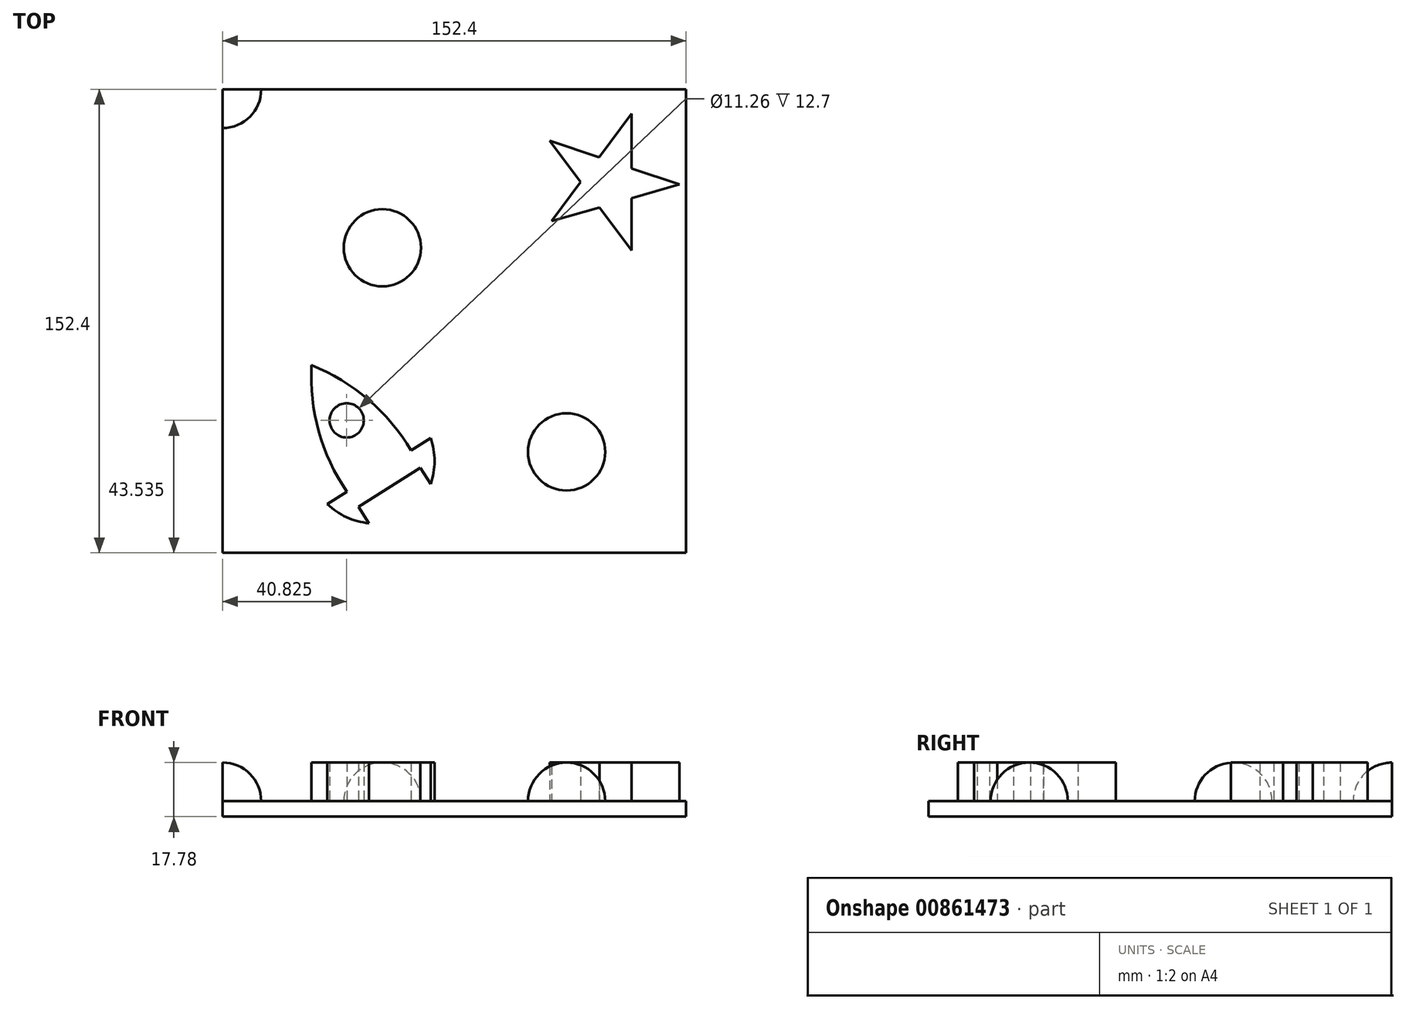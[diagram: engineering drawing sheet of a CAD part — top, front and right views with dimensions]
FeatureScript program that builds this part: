
annotation { "Feature Type Name" : "Feature", "Feature Type Description" : "" }
export const myFeature = defineFeature(function(context is Context, id is Id, definition is map)
    precondition{}
    {
        {
            var Q0;
            Q0=qCreatedBy(makeId("Top.planeOp"),FACE);
            var sketch = newSketch(context, id + "F0", { "sketchPlane" : qUnion([Q0])});
            skLineSegment(sketch, "E0.bottom", {"start": v(76.2, -76.2) * mm, "end": v(-76.2, -76.2) * mm});
            skLineSegment(sketch, "E0.top", {"start": v(76.2, 76.2) * mm, "end": v(-76.2, 76.2) * mm});
            skLineSegment(sketch, "E0.left", {"start": v(76.2, -76.2) * mm, "end": v(76.2, 76.2) * mm});
            skLineSegment(sketch, "E0.right", {"start": v(-76.2, -76.2) * mm, "end": v(-76.2, 76.2) * mm});
            skPoint(sketch, "E0.middle", {"position": v(0, 0) * mm});
            skLineSegment(sketch, "E1", {"start": v(0, 76.2) * mm, "end": v(0, -76.2) * mm, "construction": true});
            skLineSegment(sketch, "E2", {"start": v(-76.2, 0) * mm, "end": v(76.2, 0) * mm, "construction": true});
            skSolve(sketch);
        }
        {
            assignVariable(context, id + "F1", {"name" : "height", "anyValue" : 5.08 * mm});
        }
        {
            var Q0;
            Q0=makeQuery(id+"F0.imprint","IMPRINT",FACE,{"disambiguationData":[TD([[makeQuery(id+"F0.imprint","IMPRINT",EDGE,{"derivedFrom":sQuery(id+"F0.wireOp",EDGE,"E0.bottom")}),-1.0]])]});
            extrude(context, id + "F2", {"entities" : qUnion([Q0]), "depth" : getVariable(context, 'height'), "offsetDistance" : 25.4 * mm});
        }
        {
            assignVariable(context, id + "F3", {"name" : "height2", "anyValue" : 12.7 * mm});
        }
        {
            var Q0;
            Q0=makeQuery(id+"F2.opExtrude","CAP_FACE",FACE,{"disambiguationData":[OSD([sQuery(id+"F0.wireOp",EDGE,"E0.bottom"),sQuery(id+"F0.wireOp",EDGE,"E0.top"),sQuery(id+"F0.wireOp",EDGE,"E0.left"),sQuery(id+"F0.wireOp",EDGE,"E0.right")])],"isStart":false});
            var sketch = newSketch(context, id + "F4", { "sketchPlane" : qUnion([Q0])});
            skArc(sketch, "E3", {"start": v(49.62, -43.02) * mm, "mid": v(36.92, -30.32) * mm, "end": v(24.22, -43.02) * mm});
            skArc(sketch, "E4", {"start": v(-76.2, 63.5) * mm, "mid": v(-67.22, 67.22) * mm, "end": v(-63.5, 76.2) * mm});
            skLineSegment(sketch, "E5", {"start": v(49.62, -43.02) * mm, "end": v(24.22, -43.02) * mm});
            skLineSegment(sketch, "E6", {"start": v(-36.35, 24.1) * mm, "end": v(-10.95, 24.1) * mm});
            skArc(sketch, "E7", {"start": v(-10.95, 24.1) * mm, "mid": v(-23.65, 36.8) * mm, "end": v(-36.35, 24.1) * mm});
            skLineSegment(sketch, "E8", {"start": v(31.39, 59.27) * mm, "end": v(47.57, 53.82) * mm});
            skLineSegment(sketch, "E9", {"start": v(74, 44.9) * mm, "end": v(58.26, 40.4) * mm});
            skLineSegment(sketch, "E10", {"start": v(31.97, 32.85) * mm, "end": v(41.52, 45.68) * mm});
            skLineSegment(sketch, "E11", {"start": v(58.26, 68.18) * mm, "end": v(58.26, 50.22) * mm});
            skLineSegment(sketch, "E12", {"start": v(58.26, 23.21) * mm, "end": v(47.71, 37.37) * mm});
            skLineSegment(sketch, "E13.trimOffspring", {"start": v(41.52, 45.68) * mm, "end": v(31.39, 59.27) * mm});
            skLineSegment(sketch, "E14.trimOffspring", {"start": v(47.71, 37.37) * mm, "end": v(31.97, 32.85) * mm});
            skLineSegment(sketch, "E15.trimOffspring", {"start": v(58.26, 40.4) * mm, "end": v(58.26, 23.21) * mm});
            skLineSegment(sketch, "E16.trimOffspring", {"start": v(58.26, 50.22) * mm, "end": v(74, 44.9) * mm});
            skLineSegment(sketch, "E17.trimOffspring", {"start": v(47.57, 53.82) * mm, "end": v(58.26, 68.18) * mm});
            skLineSegment(sketch, "E18", {"start": v(-31.46, -61.14) * mm, "end": v(-11.2, -48.23) * mm});
            skLineSegment(sketch, "E19", {"start": v(-21.33, -54.69) * mm, "end": v(-46.94, -14.53) * mm, "construction": true});
            skArc(sketch, "E20", {"start": v(-46.94, -14.53) * mm, "mid": v(-43.64, -39.3) * mm, "end": v(-31.46, -61.14) * mm});
            skArc(sketch, "E21", {"start": v(-11.2, -48.23) * mm, "mid": v(-25.87, -27.98) * mm, "end": v(-46.94, -14.53) * mm});
            skLineSegment(sketch, "E22", {"start": v(-11.2, -48.23) * mm, "end": v(-7.8, -53.58) * mm});
            skLineSegment(sketch, "E23", {"start": v(-31.46, -61.14) * mm, "end": v(-28.04, -66.5) * mm});
            skLineSegment(sketch, "E24", {"start": v(-14.18, -42.6) * mm, "end": v(-35.31, -56.07) * mm, "construction": true});
            skLineSegment(sketch, "E25", {"start": v(-14.18, -42.6) * mm, "end": v(-7.72, -38.48) * mm});
            skLineSegment(sketch, "E26", {"start": v(-35.31, -56.07) * mm, "end": v(-41.77, -60.19) * mm});
            skArc(sketch, "E27", {"start": v(-7.8, -53.58) * mm, "mid": v(-6.5, -46.04) * mm, "end": v(-7.72, -38.48) * mm});
            skArc(sketch, "E28", {"start": v(-41.77, -60.19) * mm, "mid": v(-35.43, -64.49) * mm, "end": v(-28.04, -66.5) * mm});
            skCircle(sketch, "E29", {"center": v(-35.38, -32.66) * mm, "radius": 5.63 * mm});
            skSolve(sketch);
        }
        {
            var Q0;
            {var subQ0=sQuery(id+"F4.wireOp",EDGE,"E4");var subQ1=makeQuery(id+"F2.opExtrude","CAP_EDGE",EDGE,{"disambiguationData":[OSD([sQuery(id+"F0.wireOp",EDGE,"E0.right")])],"isStart":false});var subQ2=makeQuery(id+"F4.imprint","INTERSECT",VERTEX,{"derivedFrom":[subQ1,subQ0]});Q0=makeQuery(id+"F4.imprint","IMPRINT",FACE,{"disambiguationData":[TD([[makeQuery(id+"F4.imprint","IMPRINT",EDGE,{"disambiguationData":[TD([[subQ2,-1.0]])],"derivedFrom":subQ0}),1.0]])]});}
            var Q1;
            Q1=makeQuery(id+"F2.opExtrude","CAP_EDGE",EDGE,{"disambiguationData":[OSD([sQuery(id+"F0.wireOp",EDGE,"E0.right")])],"isStart":false});
            revolve(context, id + "F5", {"operationType" : NewBodyOperationType.ADD, "surfaceOperationType" : NewSurfaceOperationType.NEW, "entities" : qUnion([Q0]), "axis" : qUnion([Q1]), "revolveType" : RevolveType.ONE_DIRECTION, "oppositeDirection" : true, "angle" : 90 * degree});
        }
        {
            var Q0;
            Q0=makeQuery(id+"F4.imprint","IMPRINT",FACE,{"disambiguationData":[TD([[makeQuery(id+"F4.imprint","IMPRINT",EDGE,{"derivedFrom":sQuery(id+"F4.wireOp",EDGE,"E3")}),1.0]])]});
            var Q1;
            Q1=sQuery(id+"F4.wireOp",EDGE,"E5");
            revolve(context, id + "F6", {"operationType" : NewBodyOperationType.ADD, "surfaceOperationType" : NewSurfaceOperationType.NEW, "entities" : qUnion([Q0]), "axis" : qUnion([Q1]), "revolveType" : RevolveType.ONE_DIRECTION, "oppositeDirection" : true, "angle" : 180 * degree});
        }
        {
            var Q0;
            Q0=makeQuery(id+"F4.imprint","IMPRINT",FACE,{"disambiguationData":[TD([[makeQuery(id+"F4.imprint","IMPRINT",EDGE,{"derivedFrom":sQuery(id+"F4.wireOp",EDGE,"E6")}),1.0]])]});
            var Q1;
            Q1=sQuery(id+"F4.wireOp",EDGE,"E6");
            revolve(context, id + "F7", {"operationType" : NewBodyOperationType.ADD, "surfaceOperationType" : NewSurfaceOperationType.NEW, "entities" : qUnion([Q0]), "axis" : qUnion([Q1]), "revolveType" : RevolveType.ONE_DIRECTION, "angle" : 180 * degree});
        }
        {
            var Q0;
            Q0=makeQuery(id+"F4.imprint","IMPRINT",FACE,{"disambiguationData":[TD([[makeQuery(id+"F4.imprint","IMPRINT",EDGE,{"derivedFrom":sQuery(id+"F4.wireOp",EDGE,"E8")}),-1.0]])]});
            var Q1;
            {var subQ1=sQuery(id+"F4.wireOp",EDGE,"E18");Q1=makeQuery(id+"F4.imprint","IMPRINT",FACE,{"disambiguationData":[TD([[makeQuery(id+"F4.imprint","IMPRINT",EDGE,{"derivedFrom":subQ1}),1.0]])]});}
            var Q2;
            {var subQ0=sQuery(id+"F4.wireOp",EDGE,"E22");Q2=makeQuery(id+"F4.imprint","IMPRINT",FACE,{"disambiguationData":[TD([[makeQuery(id+"F4.imprint","IMPRINT",EDGE,{"derivedFrom":subQ0}),1.0]])]});}
            var Q3;
            {var subQ0=sQuery(id+"F4.wireOp",EDGE,"E23");Q3=makeQuery(id+"F4.imprint","IMPRINT",FACE,{"disambiguationData":[TD([[makeQuery(id+"F4.imprint","IMPRINT",EDGE,{"derivedFrom":subQ0}),-1.0]])]});}
            extrude(context, id + "F8", {"entities" : qUnion([Q0, Q1, Q2, Q3]), "operationType" : NewBodyOperationType.ADD, "depth" : getVariable(context, 'height2'), "offsetDistance" : 25.4 * mm});
        }
    });
